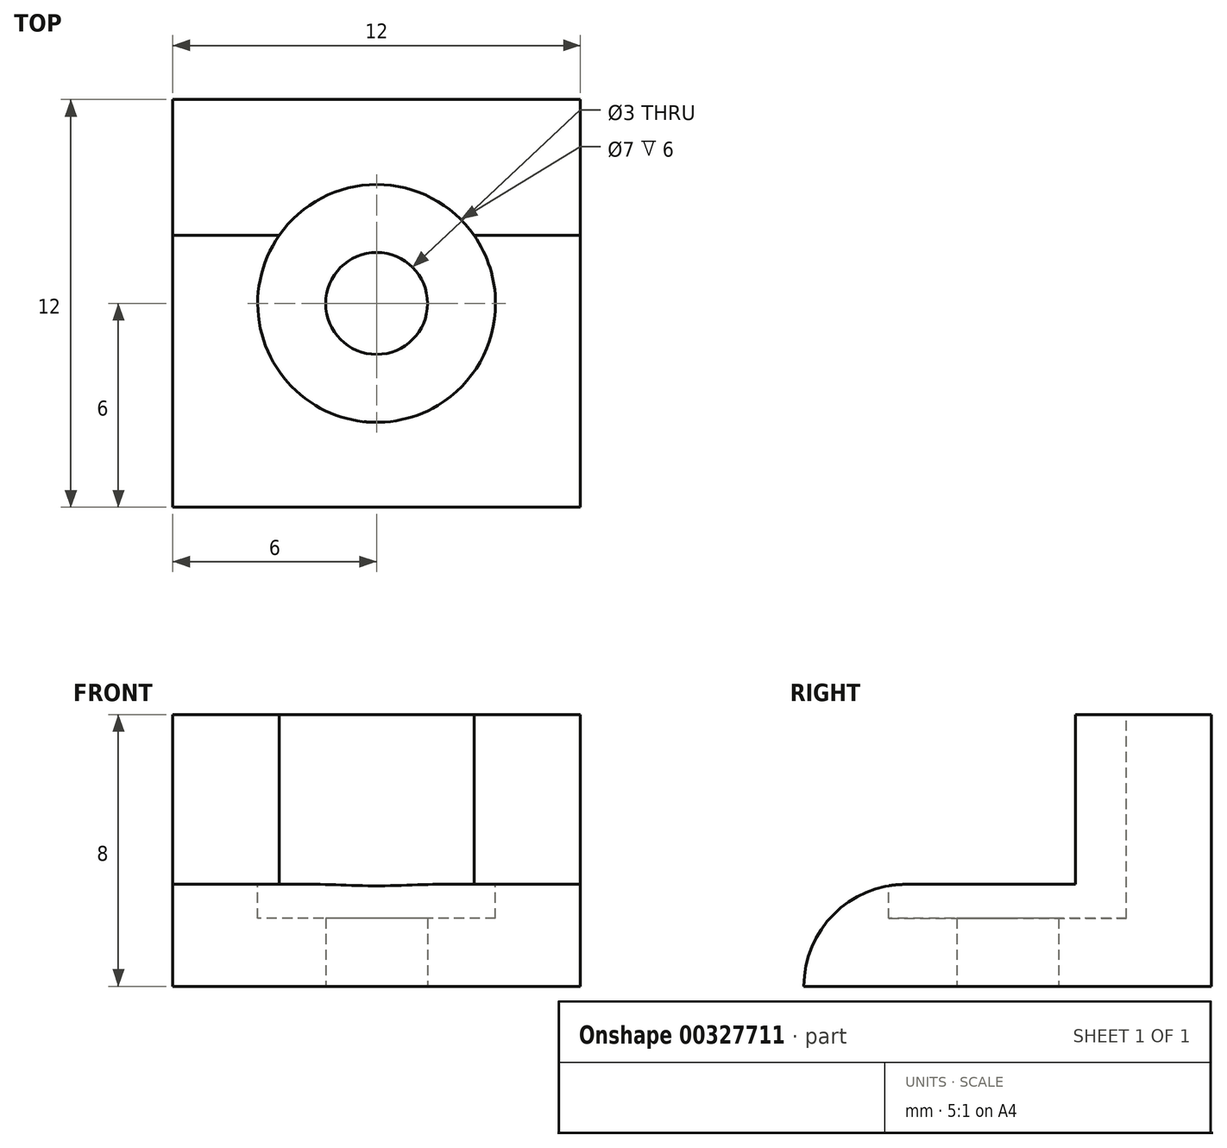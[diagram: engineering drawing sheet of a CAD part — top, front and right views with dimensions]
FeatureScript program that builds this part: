
annotation { "Feature Type Name" : "Feature", "Feature Type Description" : "" }
export const myFeature = defineFeature(function(context is Context, id is Id, definition is map)
    precondition{}
    {
        {
            var Q0;
            Q0=qCreatedBy(makeId("Top.planeOp"),FACE);
            var sketch = newSketch(context, id + "F0", { "sketchPlane" : qUnion([Q0])});
            skLineSegment(sketch, "E0.bottom", {"start": v(6, -6) * mm, "end": v(-6, -6) * mm});
            skLineSegment(sketch, "E0.top", {"start": v(6, 6) * mm, "end": v(-6, 6) * mm});
            skLineSegment(sketch, "E0.left", {"start": v(6, -6) * mm, "end": v(6, 6) * mm});
            skLineSegment(sketch, "E0.right", {"start": v(-6, -6) * mm, "end": v(-6, 6) * mm});
            skPoint(sketch, "E0.middle", {"position": v(0, 0) * mm});
            skCircle(sketch, "E1", {"center": v(0, 0) * mm, "radius": 1.5 * mm});
            skSolve(sketch);
        }
        {
            var Q0;
            Q0=makeQuery(id+"F0.imprint","IMPRINT",FACE,{"disambiguationData":[TD([[makeQuery(id+"F0.imprint","IMPRINT",EDGE,{"derivedFrom":sQuery(id+"F0.wireOp",EDGE,"E0.bottom")}),-1.0]])]});
            extrude(context, id + "F1", {"entities" : qUnion([Q0]), "depth" : 3 * mm});
        }
        {
            var Q0;
            Q0=makeQuery(id+"F1.opExtrude","CAP_FACE",FACE,{"disambiguationData":[OSD([sQuery(id+"F0.wireOp",EDGE,"E0.bottom"),sQuery(id+"F0.wireOp",EDGE,"E0.top"),sQuery(id+"F0.wireOp",EDGE,"E0.left"),sQuery(id+"F0.wireOp",EDGE,"E0.right"),sQuery(id+"F0.wireOp",EDGE,"E1")])],"isStart":false});
            var sketch = newSketch(context, id + "F2", { "sketchPlane" : qUnion([Q0])});
            skLineSegment(sketch, "E2.bottom", {"start": v(-6, 6) * mm, "end": v(6, 6) * mm});
            skLineSegment(sketch, "E2.top", {"start": v(-6, 2) * mm, "end": v(6, 2) * mm});
            skLineSegment(sketch, "E2.left", {"start": v(-6, 6) * mm, "end": v(-6, 2) * mm});
            skLineSegment(sketch, "E2.right", {"start": v(6, 6) * mm, "end": v(6, 2) * mm});
            skSolve(sketch);
        }
        {
            var Q0;
            Q0=makeQuery(id+"F2.imprint","IMPRINT",FACE,{"disambiguationData":[TD([[makeQuery(id+"F2.imprint","IMPRINT",EDGE,{"derivedFrom":sQuery(id+"F2.wireOp",EDGE,"E2.bottom")}),1.0]])]});
            extrude(context, id + "F3", {"entities" : qUnion([Q0]), "operationType" : NewBodyOperationType.ADD, "depth" : 5 * mm});
        }
        {
            var Q0;
            Q0=makeQuery(id+"F3.opExtrude","CAP_FACE",FACE,{"disambiguationData":[OSD([sQuery(id+"F2.wireOp",EDGE,"E2.bottom"),sQuery(id+"F2.wireOp",EDGE,"E2.top"),sQuery(id+"F2.wireOp",EDGE,"E2.left"),sQuery(id+"F2.wireOp",EDGE,"E2.right")])],"isStart":false});
            var sketch = newSketch(context, id + "F4", { "sketchPlane" : qUnion([Q0])});
            skCircle(sketch, "E3", {"center": v(0, 0) * mm, "radius": 3.5 * mm});
            skSolve(sketch);
        }
        {
            var Q0;
            Q0=makeQuery(id+"F1.opExtrude","CAP_EDGE",EDGE,{"disambiguationData":[OSD([sQuery(id+"F0.wireOp",EDGE,"E0.bottom")])],"isStart":false});
            fillet(context, id + "F5", {"entities" : qUnion([Q0]), "radius" : 3 * mm, "tangentPropagation" : true, "allowEdgeOverflow" : false});
        }
        {
            var Q0;
            {var subQ0=sQuery(id+"F4.wireOp",EDGE,"E3");var subQ1=makeQuery(id+"F3.opExtrude","CAP_EDGE",EDGE,{"disambiguationData":[OSD([sQuery(id+"F2.wireOp",EDGE,"E2.top")])],"isStart":false});var subQ2=makeQuery(id+"F4.imprint","INTERSECT",VERTEX,{"disambiguationData":[OD(0.0)],"derivedFrom":[subQ1,subQ0]});Q0=makeQuery(id+"F4.imprint","IMPRINT",FACE,{"disambiguationData":[TD([[makeQuery(id+"F4.imprint","IMPRINT",EDGE,{"disambiguationData":[TD([[subQ2,-1.0]])],"derivedFrom":subQ0}),1.0]])]});}
            var Q1;
            {var subQ0=sQuery(id+"F4.wireOp",EDGE,"E3");var subQ1=makeQuery(id+"F3.opExtrude","CAP_EDGE",EDGE,{"disambiguationData":[OSD([sQuery(id+"F2.wireOp",EDGE,"E2.top")])],"isStart":false});var subQ2=makeQuery(id+"F4.imprint","INTERSECT",VERTEX,{"disambiguationData":[OD(0.0)],"derivedFrom":[subQ1,subQ0]});Q1=makeQuery(id+"F4.imprint","IMPRINT",FACE,{"disambiguationData":[TD([[makeQuery(id+"F4.imprint","IMPRINT",EDGE,{"disambiguationData":[TD([[subQ2,1.0]])],"derivedFrom":subQ0}),1.0]])]});}
            extrude(context, id + "F6", {"entities" : qUnion([Q0, Q1]), "operationType" : NewBodyOperationType.REMOVE, "oppositeDirection" : true, "depth" : 6 * mm});
        }
    });
